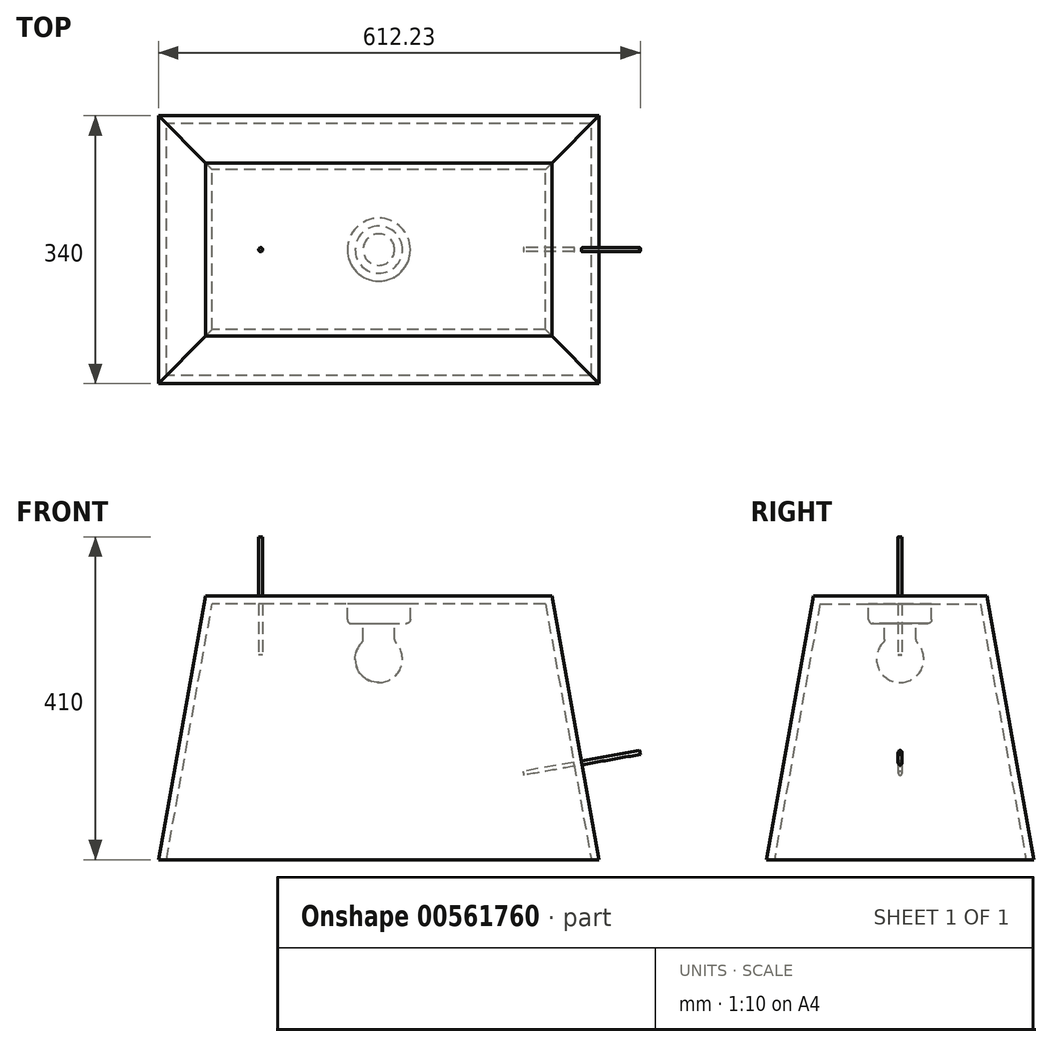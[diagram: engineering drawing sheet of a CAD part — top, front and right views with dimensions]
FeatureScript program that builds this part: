
annotation { "Feature Type Name" : "Feature", "Feature Type Description" : "" }
export const myFeature = defineFeature(function(context is Context, id is Id, definition is map)
    precondition{}
    {
        {
            var Q0;
            Q0=qCreatedBy(makeId("Top.planeOp"),FACE);
            cPlane(context, id + "F0", {"entities" : qUnion([Q0]), "cplaneType" : CPlaneType.OFFSET, "offset" : 167.5 * mm, "width" : 150 * mm, "height" : 150 * mm});
        }
        {
            var Q0;
            Q0=qCreatedBy(makeId("Top.planeOp"),FACE);
            cPlane(context, id + "F1", {"entities" : qUnion([Q0]), "cplaneType" : CPlaneType.OFFSET, "offset" : 167.5 * mm, "oppositeDirection" : true, "width" : 150 * mm, "height" : 150 * mm});
        }
        {
            var Q0;
            Q0=qCreatedBy(id+"F0.planeOp",FACE);
            var sketch = newSketch(context, id + "F2", { "sketchPlane" : qUnion([Q0])});
            skLineSegment(sketch, "E0.bottom", {"start": v(220, 110) * mm, "end": v(-220, 110) * mm});
            skLineSegment(sketch, "E0.top", {"start": v(220, -110) * mm, "end": v(-220, -110) * mm});
            skLineSegment(sketch, "E0.left", {"start": v(220, 110) * mm, "end": v(220, -110) * mm});
            skLineSegment(sketch, "E0.right", {"start": v(-220, 110) * mm, "end": v(-220, -110) * mm});
            skPoint(sketch, "E0.middle", {"position": v(0, 0) * mm});
            skSolve(sketch);
        }
        {
            var Q0;
            Q0=qCreatedBy(id+"F1.planeOp",FACE);
            var sketch = newSketch(context, id + "F3", { "sketchPlane" : qUnion([Q0])});
            skLineSegment(sketch, "E1.bottom", {"start": v(280, -170) * mm, "end": v(-280, -170) * mm});
            skLineSegment(sketch, "E1.top", {"start": v(280, 170) * mm, "end": v(-280, 170) * mm});
            skLineSegment(sketch, "E1.left", {"start": v(280, -170) * mm, "end": v(280, 170) * mm});
            skLineSegment(sketch, "E1.right", {"start": v(-280, -170) * mm, "end": v(-280, 170) * mm});
            skPoint(sketch, "E1.middle", {"position": v(0, 0) * mm});
            skSolve(sketch);
        }
        {
            var Q0;
            Q0=makeQuery(id+"F3.imprint","IMPRINT",FACE,{"disambiguationData":[TD([[makeQuery(id+"F3.imprint","IMPRINT",EDGE,{"derivedFrom":sQuery(id+"F3.wireOp",EDGE,"E1.bottom")}),-1.0]])]});
            var Q1;
            Q1=makeQuery(id+"F2.imprint","IMPRINT",FACE,{"disambiguationData":[TD([[makeQuery(id+"F2.imprint","IMPRINT",EDGE,{"derivedFrom":sQuery(id+"F2.wireOp",EDGE,"E0.bottom")}),1.0]])]});
            loft(context, id + "F4", {"sheetProfilesArray" : [{ "sheetProfileEntities" : qUnion([Q0]) }, { "sheetProfileEntities" : qUnion([Q1]) }]});
        }
        {
            var Q0;
            Q0=makeQuery(id+"F4.opLoft","CAP_FACE",FACE,{"disambiguationData":[OSD([makeQuery(id+"F3.imprint","IMPRINT",FACE,{"disambiguationData":[TD([[makeQuery(id+"F3.imprint","IMPRINT",EDGE,{"derivedFrom":sQuery(id+"F3.wireOp",EDGE,"E1.bottom")}),-1.0]])]})])],"isStart":true});
            shell(context, id + "F5", {"entities" : qUnion([Q0]), "thickness" : 10 * mm});
        }
        {
            var Q0;
            Q0=makeQuery(id+"F4.opLoft","CAP_FACE",FACE,{"disambiguationData":[OSD([makeQuery(id+"F2.imprint","IMPRINT",FACE,{"disambiguationData":[TD([[makeQuery(id+"F2.imprint","IMPRINT",EDGE,{"derivedFrom":sQuery(id+"F2.wireOp",EDGE,"E0.bottom")}),1.0]])]})])],"isStart":true});
            var sketch = newSketch(context, id + "F6", { "sketchPlane" : qUnion([Q0])});
            skCircle(sketch, "E2", {"center": v(-150, 0) * mm, "radius": 2.5 * mm});
            skSolve(sketch);
        }
        {
            var Q0;
            Q0=makeQuery(id+"F4.opLoft","SWEPT_FACE",FACE,{"disambiguationData":[OSD([sQuery(id+"F2.wireOp",EDGE,"E0.bottom"),sQuery(id+"F2.wireOp",EDGE,"E0.top"),sQuery(id+"F2.wireOp",EDGE,"E0.left"),sQuery(id+"F3.wireOp",EDGE,"E1.bottom"),sQuery(id+"F3.wireOp",EDGE,"E1.top"),sQuery(id+"F3.wireOp",EDGE,"E1.left")])]});
            var sketch = newSketch(context, id + "F7", { "sketchPlane" : qUnion([Q0])});
            skCircle(sketch, "E3", {"center": v(0, -89.24) * mm, "radius": 2.5 * mm});
            skSolve(sketch);
        }
        {
            var Q0;
            Q0=makeQuery(id+"F5.opShell","OFFSET_FACE",FACE,{"disambiguationData":[OSD([makeQuery(id+"F2.imprint","IMPRINT",FACE,{"disambiguationData":[TD([[makeQuery(id+"F2.imprint","IMPRINT",EDGE,{"derivedFrom":sQuery(id+"F2.wireOp",EDGE,"E0.bottom")}),1.0]])]})])]});
            var sketch = newSketch(context, id + "F8", { "sketchPlane" : qUnion([Q0])});
            skCircle(sketch, "E4", {"center": v(0, 0) * mm, "radius": 40 * mm});
            skSolve(sketch);
        }
        {
            var Q0;
            Q0=makeQuery(id+"F8.imprint","IMPRINT",FACE,{"disambiguationData":[TD([[makeQuery(id+"F8.imprint","IMPRINT",EDGE,{"derivedFrom":sQuery(id+"F8.wireOp",EDGE,"E4")}),1.0]])]});
            extrude(context, id + "F9", {"entities" : qUnion([Q0]), "operationType" : NewBodyOperationType.ADD, "depth" : 25 * mm, "offsetDistance" : 25 * mm});
        }
        {
            var Q0;
            Q0=makeQuery(id+"F9.opExtrude","CAP_FACE",FACE,{"disambiguationData":[OSD([sQuery(id+"F8.wireOp",EDGE,"E4")])],"isStart":false});
            var sketch = newSketch(context, id + "F10", { "sketchPlane" : qUnion([Q0])});
            skCircle(sketch, "E5", {"center": v(0, 0) * mm, "radius": 20 * mm});
            skSolve(sketch);
        }
        {
            var Q0;
            Q0=makeQuery(id+"F10.imprint","IMPRINT",FACE,{"disambiguationData":[TD([[makeQuery(id+"F10.imprint","IMPRINT",EDGE,{"derivedFrom":sQuery(id+"F10.wireOp",EDGE,"E5")}),1.0]])]});
            extrude(context, id + "F11", {"entities" : qUnion([Q0]), "operationType" : NewBodyOperationType.ADD, "depth" : 25 * mm, "offsetDistance" : 25 * mm});
        }
        {
            var Q0;
            Q0=makeQuery(id+"F11.opExtrude","SWEPT_FACE",FACE,{"disambiguationData":[OSD([sQuery(id+"F10.wireOp",EDGE,"E5")])]});
            cPlane(context, id + "F12", {"entities" : qUnion([Q0]), "cplaneType" : CPlaneType.LINE_ANGLE, "offset" : 25 * mm, "angle" : 90 * degree, "oppositeDirection" : true, "width" : 150 * mm, "height" : 150 * mm});
        }
        {
            var Q0;
            Q0=qCreatedBy(id+"F12.planeOp",FACE);
            var sketch = newSketch(context, id + "F13", { "sketchPlane" : qUnion([Q0])});
            skArc(sketch, "E6", {"start": v(0, 57.5) * mm, "mid": v(30, 87.5) * mm, "end": v(0, 117.5) * mm});
            skLineSegment(sketch, "E7", {"start": v(0, 117.5) * mm, "end": v(0, 57.5) * mm});
            skSolve(sketch);
        }
        {
            var Q0;
            Q0=makeQuery(id+"F13.imprint","IMPRINT",FACE,{"disambiguationData":[TD([[makeQuery(id+"F13.imprint","IMPRINT",EDGE,{"derivedFrom":sQuery(id+"F13.wireOp",EDGE,"E6")}),1.0]])]});
            var Q1;
            Q1=sQuery(id+"F13.wireOp",EDGE,"E7");
            revolve(context, id + "F14", {"operationType" : NewBodyOperationType.ADD, "entities" : qUnion([Q0]), "axis" : qUnion([Q1]), "revolveType" : RevolveType.FULL});
        }
        {
            var Q0;
            Q0=makeQuery(id+"F11.opExtrude","CAP_EDGE",EDGE,{"disambiguationData":[OSD([sQuery(id+"F10.wireOp",EDGE,"E5")])],"isStart":true});
            var Q1;
            Q1=makeQuery(id+"F9.opExtrude","CAP_EDGE",EDGE,{"disambiguationData":[OSD([sQuery(id+"F8.wireOp",EDGE,"E4")])],"isStart":false});
            var Q2;
            Q2=makeQuery(id+"F14.boolean.opBoolean","INTERSECT",EDGE,{"derivedFrom":[makeQuery(id+"F11.opExtrude","SWEPT_FACE",FACE,{"disambiguationData":[OSD([sQuery(id+"F10.wireOp",EDGE,"E5")])]}),makeQuery(id+"F14.opRevolve","SWEPT_FACE",FACE,{"disambiguationData":[OSD([sQuery(id+"F13.wireOp",EDGE,"E6")])]})]});
            var Q3;
            Q3=makeQuery(id+"F9.opExtrude","CAP_EDGE",EDGE,{"disambiguationData":[OSD([sQuery(id+"F8.wireOp",EDGE,"E4")])],"isStart":true});
            fillet(context, id + "F15", {"entities" : qUnion([Q0, Q1, Q2, Q3]), "radius" : 5 * mm, "tangentPropagation" : true, "allowEdgeOverflow" : false});
        }
        {
            var Q0;
            Q0=makeQuery(id+"F6.imprint","IMPRINT",FACE,{"disambiguationData":[TD([[makeQuery(id+"F6.imprint","IMPRINT",EDGE,{"derivedFrom":sQuery(id+"F6.wireOp",EDGE,"E2")}),1.0]])]});
            extrude(context, id + "F16", {"entities" : qUnion([Q0]), "operationType" : NewBodyOperationType.ADD, "endBound" : BoundingType.SYMMETRIC, "depth" : 150 * mm, "offsetDistance" : 25 * mm});
        }
        {
            var Q0;
            Q0=makeQuery(id+"F7.imprint","IMPRINT",FACE,{"disambiguationData":[TD([[makeQuery(id+"F7.imprint","IMPRINT",EDGE,{"derivedFrom":sQuery(id+"F7.wireOp",EDGE,"E3")}),1.0]])]});
            extrude(context, id + "F17", {"entities" : qUnion([Q0]), "operationType" : NewBodyOperationType.ADD, "endBound" : BoundingType.SYMMETRIC, "depth" : 150 * mm, "offsetDistance" : 25 * mm});
        }
    });
